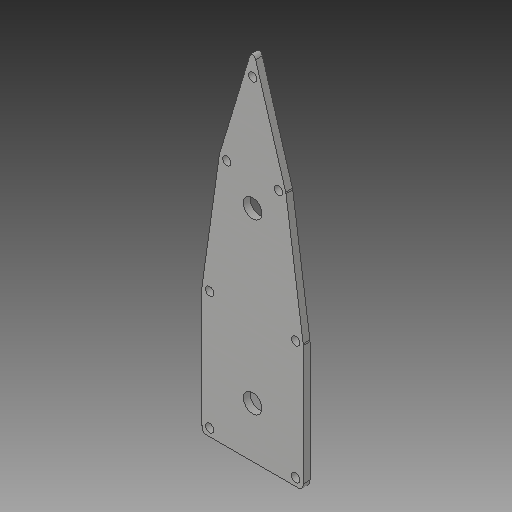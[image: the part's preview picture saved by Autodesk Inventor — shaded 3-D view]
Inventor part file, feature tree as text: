
AUTODESK INVENTOR PART (.ipt)
format: ipt  version: 2018 (Build 220112000, 112)  size: 233,984 bytes
history: native  units: mm
features: other x7, sketch x2, plane x1, sheet_metal_op x1, reference x1, projected_geometry x1
ambient origin geometry x8: Origin, YZ Plane, XZ Plane, XY Plane, X Axis, Y Axis, Z Axis, Center Point
bodies: Solid1 (feature_tree)
feature tree (13):
  plane  "Work Plane1"
  sheet_metal_op  "Face1"
  sketch  "Sketch1"  dims[d0=8.0mm]
  reference  "Reference1"
  other  "Plate1"
  sketch  "Sketch2"  dims[d1=22.0mm d2=22.0mm d3=10.0mm d4=10.0mm d5=10.0mm d6=10.0mm d7=10.0mm d8=10.0mm d9=10.0mm d10=10.0mm d11=10.0mm d12=10.0mm d13=10.0mm d14=10.0mm d15=9.0mm d16=9.0mm d17=4.0mm d18=9.0mm d19=9.0mm d20=9.0mm d21=9.0mm d22=9.0mm d23=9.0mm d24=9.0mm d25=9.0mm d26=9.0mm d27=9.0mm d28=9.0mm d29=9.0mm d30=60.0mm d31=60.0mm d33=200.0mm d34=8.0mm d35=0.0mm]
  projected_geometry  "Projected Loop1"
  other  "zinkdrænshuller"
  parser-record x1  (decoder bookkeeping rows leaked as tree rows — omitted from the tree; the rows remain in map.json)
  other  "modul bund.iam"
  other  "vange bund:1"
  other  "Definition1"
  other  "plade bund:1"
note: 1 file-system path scrubbed to <path> (originals preserved in map.json)
